# Revit family: Shower-Handshower-KOHLER-SHIFT-K-21336T
name_source: partatom
category: Plumbing Fixtures
revit_build: Autodesk Revit 2017 (Build: 20160225_1515(x64)
units: mm (PartAtom-declared; Revit-internal decimal feet)

## family parameters
Cut with Voids When Loaded = No
Host = Face
OmniClass Number = 23.31.17.00
OmniClass Title = Showers
Part Type = Normal
Room Calculation Point = No
Round Connector Dimension = Use Diameter
Shared = No

## types (9) — shared parameters
ADA Compliant = No
Assembly Code = D2010
CW Connection = No
Cold Water Inlet = Cold Water Inlet
Date Modified = 20/08/2020
Default Elevation = 36"
Description = Multifunctional Fashion Rod Handheld Shower-Square
Drain Included = No
Flow Rate = 0 GPM
HW Connection = Yes
Height = 9 13/16"
Hot Water Inlet = Hot Water Inlet
Length = 1 1/8"
Manufacturer = KOHLER Co.
Master Format 2014 = 22 41 39
Master Format 2014 Name = Residential Faucets, Supplies, and Trim
Material = Premium Metal Construction
Pressure = 0.00 psi
Product Documentation Link = https://files.kohler.com.cn
Product Name = SHIFT
Product Page URL = https://www.kohler.com.cn
Tempered Water Inlet = Tempered Water Inlet
URL = http://www.kohler.com.cn
Vent Connection = No
Waste Connection = No
Waste Water Outlet = Waste Water Outlet
WaterSense Certified = No
Width = 1 1/8"

## per-type parameters (varying)
| type | Finish | Model | Type |
| CP-Polished Chrome | Kohler-Metal-CP-Polished_Chrome | K-21336T-CP | 1 |
| AF-Vibrant French Gold | Kohler-Metal-AF-Vibrant_French_Gold | K-21336T-AF | 2 |
| SN-Champagne Gold | Kohler-Metal-SN-Vibrant_Polished_Nickel | K-21336T-SN | 3 |
| BV-Brushed Bronze | Kohler-Metal-BV-Brushed_Bronze | K-21336T-BV | 4 |
| BN-Roman Silver | Kohler-Metal-BN-Vibrant_Brushed_Nickel | K-21336T-BN | 5 |
| RGD-Rose Gold | Kohler-Metal-RGD-Polished_Rose_Gold | K-21336T-RGD | 6 |
| TT-Titanium Silver | Kohler-Metal-TT-Vibrant_Titanium | K-21336T-TT | 7 |
| PGD-Eternal Gold | Kohler-Metal-PGD-Modern_Polished_Gold | K-21336T-PGD | 8 |
| BL-Matte Black | Kohler-Metal-BL-Matte_Black | K-21336T-BL | 9 |

## geometry (parser evidence)
native form markers: Sweep x5
no freeform markers — native parametric forms only
